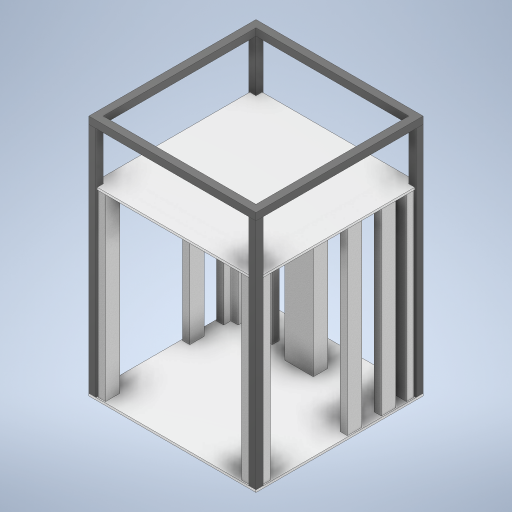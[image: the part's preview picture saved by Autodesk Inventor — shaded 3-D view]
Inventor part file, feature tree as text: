
AUTODESK INVENTOR PART (.ipt)
format: ipt  version: 2024 (Build 280153000, 153)  size: 481,792 bytes
history: native  units: mm
features: projected_geometry x8, extrude x5, sketch x3
ambient origin geometry x8: Origin, YZ Plane, XZ Plane, XY Plane, X Axis, Y Axis, Z Axis, Center Point
bodies: Solid1 (feature_tree), Solid2 (feature_tree), Solid3 (feature_tree), Solid4 (feature_tree), Solid5 (feature_tree)
feature tree (16):
  sketch  "Sketch1"  dims[d0=466.5mm d1=466.5mm]
  extrude  "Extrusion1"  Depth=466.5mm
  extrude  "Extrusion2"  Depth=20.0mm
  extrude  "Extrusion3"  Depth=40.0mm
  extrude  "Extrusion4"  Depth=3.25mm
  extrude  "Extrusion5"  Depth=3.25mm
  sketch  "Sketch2"  dims[d2=20.0mm d3=20.0mm]
  projected_geometry  "Projected Loop4"
  projected_geometry  "Projected Loop5"
  projected_geometry  "Projected Loop6"
  projected_geometry  "Projected Loop7"
  sketch  "Sketch3"  dims[d6=20.0mm d7=40.0mm d8=3.25mm d9=3.25mm d10=3.25mm d11=3.25mm d12=3.25mm d13=3.25mm d14=3.25mm d15=3.25mm d16=80.0mm d17=40.0mm d19=70.0mm d20=210.0mm d21=210.0mm d22=225.0mm d26=300.0mm d27=250.0mm d28=50.0mm d29=150.0mm d30=40.0mm d31=20.0mm d32=55.0mm d33=55.0mm d36=55.0mm d37=55.0mm d38=6.35mm d39=0.0mm d40=500.0mm d41=0.0mm d42=6.35mm d43=0.0mm d44=20.25mm d45=20.25mm d46=650.0mm d47=0.0mm d48=20.0mm d49=0.0mm d50=0.5mm d51=0.872665mm d52=0.5mm d53=0.872665mm]
  projected_geometry  "Projected Loop8"
  projected_geometry  "Projected Loop9"
  projected_geometry  "Projected Loop10"
  projected_geometry  "Projected Loop11"
